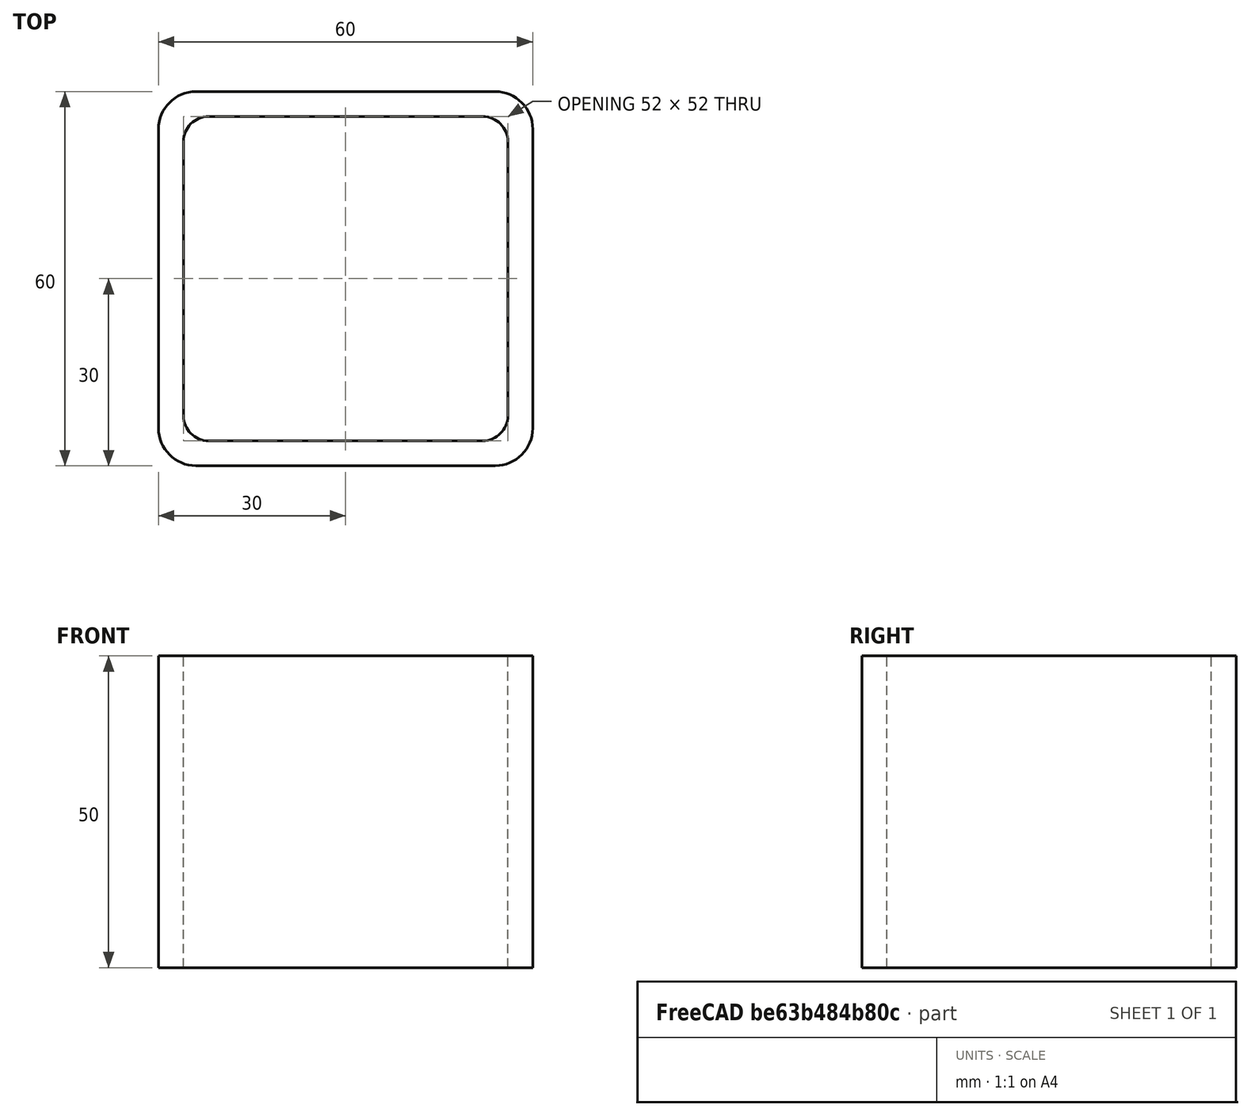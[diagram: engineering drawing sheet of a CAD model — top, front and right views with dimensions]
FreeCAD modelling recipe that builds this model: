
FCSTD DOCUMENT  (FreeCAD 0.15R4671 (Git))
Label: Square hollow section 60x60x4 EN10219 S235JRH
License: All rights reserved
LicenseURL: http://en.wikipedia.org/wiki/All_rights_reserved
objects: Sketcher::SketchObject×1, Part::Extrusion×1
note: 2 computed .brp shape members not serialized (recipe doc carries the construction recipe); baked Part::Feature solids carry a one-line shape summary decoded from their .brp

FEATURE [Sketcher::SketchObject] Sketch
  sketch-geometry (16):
    g0: LineSegment StartX=-22 StartY=26 StartZ=0 EndX=22 EndY=26 EndZ=0
    g1: LineSegment StartX=26 StartY=22 StartZ=0 EndX=26 EndY=-22 EndZ=0
    g2: LineSegment StartX=22 StartY=-26 StartZ=0 EndX=-22 EndY=-26 EndZ=0
    g3: LineSegment StartX=-26 StartY=-22 StartZ=0 EndX=-26 EndY=22 EndZ=0
    g4: LineSegment StartX=-24 StartY=30 StartZ=0 EndX=24 EndY=30 EndZ=0
    g5: LineSegment StartX=30 StartY=24 StartZ=0 EndX=30 EndY=-24 EndZ=0
    g6: LineSegment StartX=24 StartY=-30 StartZ=0 EndX=-24 EndY=-30 EndZ=0
    g7: LineSegment StartX=-30 StartY=-24 StartZ=0 EndX=-30 EndY=24 EndZ=0
    g8: ArcOfCircle CenterX=-22 CenterY=22 CenterZ=0 NormalX=0 NormalY=0 NormalZ=1 Radius=4 StartAngle=1.5708 EndAngle=3.14159
    g9: ArcOfCircle CenterX=22 CenterY=22 CenterZ=0 NormalX=0 NormalY=0 NormalZ=1 Radius=4 StartAngle=0 EndAngle=1.5708
    g10: ArcOfCircle CenterX=22 CenterY=-22 CenterZ=0 NormalX=0 NormalY=0 NormalZ=1 Radius=4 StartAngle=4.71239 EndAngle=6.28319
    g11: ArcOfCircle CenterX=-22 CenterY=-22 CenterZ=0 NormalX=0 NormalY=0 NormalZ=1 Radius=4 StartAngle=3.14159 EndAngle=4.71239
    g12: ArcOfCircle CenterX=24 CenterY=24 CenterZ=0 NormalX=0 NormalY=0 NormalZ=1 Radius=6 StartAngle=0 EndAngle=1.5708
    g13: ArcOfCircle CenterX=24 CenterY=-24 CenterZ=0 NormalX=0 NormalY=0 NormalZ=1 Radius=6 StartAngle=4.71239 EndAngle=6.28319
    g14: ArcOfCircle CenterX=-24 CenterY=-24 CenterZ=0 NormalX=0 NormalY=0 NormalZ=1 Radius=6 StartAngle=3.14159 EndAngle=4.71239
    g15: ArcOfCircle CenterX=-24 CenterY=24 CenterZ=0 NormalX=0 NormalY=0 NormalZ=1 Radius=6 StartAngle=1.5708 EndAngle=3.14159
  constraints (36):
    c: Horizontal(g2)
    c: Vertical(g3)
    c: Horizontal(g6)
    c: Vertical(g7)
    c: Tangent(g3,g8) = 1.5708
    c: Tangent(g0,g8) = 1.5708
    c: Tangent(g0,g9) = 1.5708
    c: Tangent(g1,g9) = 1.5708
    c: Tangent(g1,g10) = 1.5708
    c: Tangent(g2,g10) = 1.5708
    c: Tangent(g2,g11) = 1.5708
    c: Tangent(g3,g11) = 1.5708
    c: Tangent(g4,g12) = 1.5708
    c: Tangent(g5,g12) = 1.5708
    c: Tangent(g5,g13) = 1.5708
    c: Tangent(g6,g13) = 1.5708
    c: Tangent(g6,g14) = 1.5708
    c: Tangent(g7,g14) = 1.5708
    c: Tangent(g7,g15) = 1.5708
    c: Tangent(g4,g15) = 1.5708
    c: Equal(g9,g8)
    c: Equal(g9,g11)
    c: Equal(g9,g10)
    c: Equal(g12,g15)
    c: Equal(g12,g14)
    c: Equal(g12,g13)
    c: Symmetric(g4,g6,g-1)
    c: Symmetric(g7,g5,g-2)
    c: DistanceY(g4,g6) = -60
    c: DistanceX(g7,g5) = 60
    c: Symmetric(g3,g1,g-2)
    c: Symmetric(g0,g2,g-1)
    c: DistanceY(g0,g4) = 4
    c: DistanceX(g5,g1) = -4
    c: Radius(g9) = 4
    c: Radius(g12) = 6
FEATURE [Part::Extrusion] Extrude  label="Square hollow section 60x60x4 EN10219 S235JRH"
  Base = -> Sketch
  Dir = (0,0,50)
  Solid = true
